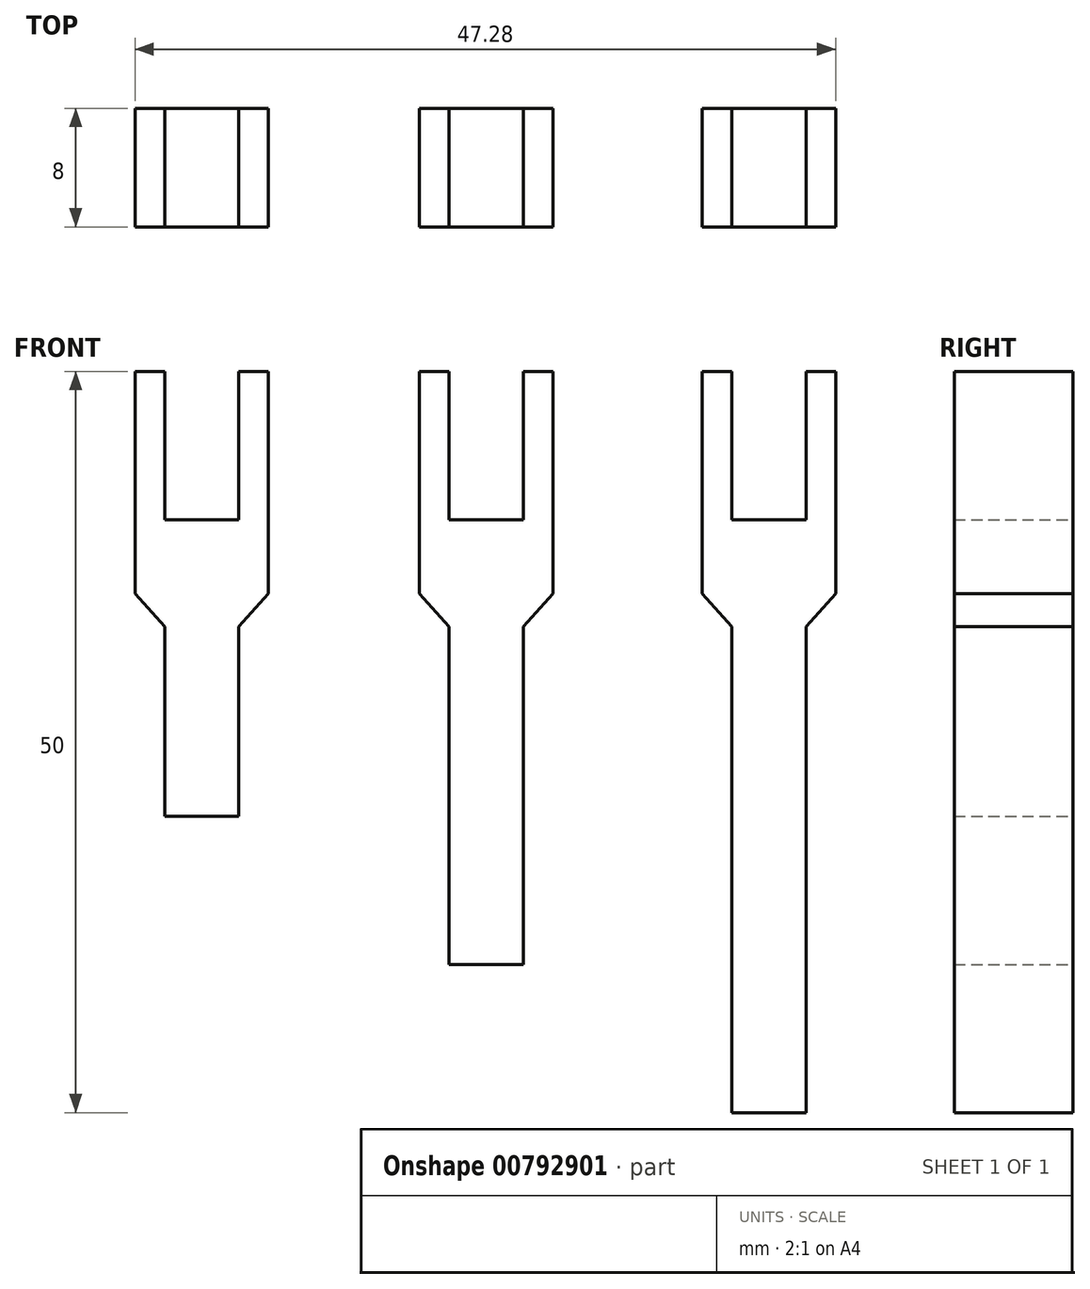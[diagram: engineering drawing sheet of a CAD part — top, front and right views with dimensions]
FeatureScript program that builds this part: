
annotation { "Feature Type Name" : "Feature", "Feature Type Description" : "" }
export const myFeature = defineFeature(function(context is Context, id is Id, definition is map)
    precondition{}
    {
        {
            var Q0;
            Q0=qCreatedBy(makeId("Front.planeOp"),FACE);
            var sketch = newSketch(context, id + "F0", { "sketchPlane" : qUnion([Q0])});
            skLineSegment(sketch, "E0.bottom", {"start": v(-2.5, -10) * mm, "end": v(2.5, -10) * mm});
            skLineSegment(sketch, "E0.top", {"start": v(-2.5, 10) * mm, "end": v(2.5, 10) * mm});
            skLineSegment(sketch, "E0.left", {"start": v(-2.5, -10) * mm, "end": v(-2.5, 2.78) * mm});
            skLineSegment(sketch, "E0.right", {"start": v(2.5, -10) * mm, "end": v(2.5, 2.78) * mm});
            skPoint(sketch, "E0.middle", {"position": v(0, 0) * mm});
            skLineSegment(sketch, "E1", {"start": v(-2.5, 10) * mm, "end": v(-2.5, 20) * mm});
            skLineSegment(sketch, "E2", {"start": v(-2.5, 20) * mm, "end": v(-4.5, 20) * mm});
            skLineSegment(sketch, "E3", {"start": v(-4.5, 20) * mm, "end": v(-4.5, 5) * mm});
            skLineSegment(sketch, "E4", {"start": v(-4.5, 5) * mm, "end": v(-2.5, 2.78) * mm});
            skLineSegment(sketch, "E5", {"start": v(0, 10) * mm, "end": v(0, 20) * mm, "construction": true});
            skLineSegment(sketch, "E6.MirrorCS", {"start": v(2.5, 10) * mm, "end": v(2.5, 20) * mm});
            skLineSegment(sketch, "E7.MirrorCS", {"start": v(2.5, 20) * mm, "end": v(4.5, 20) * mm});
            skLineSegment(sketch, "E8.MirrorCS", {"start": v(4.5, 20) * mm, "end": v(4.5, 5) * mm});
            skLineSegment(sketch, "E9.MirrorCS", {"start": v(4.5, 5) * mm, "end": v(2.5, 2.78) * mm});
            skLineSegment(sketch, "E10.top", {"start": v(16.7, 10) * mm, "end": v(21.7, 10) * mm});
            skPoint(sketch, "E10.middle", {"position": v(19.2, 0) * mm});
            skLineSegment(sketch, "E11", {"start": v(16.7, 10) * mm, "end": v(16.7, 20) * mm});
            skLineSegment(sketch, "E12", {"start": v(16.7, 20) * mm, "end": v(14.7, 20) * mm});
            skLineSegment(sketch, "E13", {"start": v(14.7, 20) * mm, "end": v(14.7, 5) * mm});
            skLineSegment(sketch, "E14", {"start": v(14.7, 5) * mm, "end": v(16.7, 2.78) * mm});
            skLineSegment(sketch, "E15", {"start": v(19.2, 10) * mm, "end": v(19.2, 20) * mm, "construction": true});
            skLineSegment(sketch, "E16.MirrorCS", {"start": v(21.7, 10) * mm, "end": v(21.7, 20) * mm});
            skLineSegment(sketch, "E17.MirrorCS", {"start": v(21.7, 20) * mm, "end": v(23.7, 20) * mm});
            skLineSegment(sketch, "E18.MirrorCS", {"start": v(23.7, 20) * mm, "end": v(23.7, 5) * mm});
            skLineSegment(sketch, "E19.MirrorCS", {"start": v(23.7, 5) * mm, "end": v(21.7, 2.78) * mm});
            skLineSegment(sketch, "E20", {"start": v(16.7, 2.78) * mm, "end": v(16.7, -20) * mm});
            skLineSegment(sketch, "E21", {"start": v(16.7, -20) * mm, "end": v(21.7, -20) * mm});
            skLineSegment(sketch, "E22", {"start": v(21.7, -20) * mm, "end": v(21.7, 2.78) * mm});
            skLineSegment(sketch, "E23.top", {"start": v(35.78, 10) * mm, "end": v(40.78, 10) * mm});
            skPoint(sketch, "E23.middle", {"position": v(38.28, 0) * mm});
            skLineSegment(sketch, "E24", {"start": v(35.78, 10) * mm, "end": v(35.78, 20) * mm});
            skLineSegment(sketch, "E25", {"start": v(35.78, 20) * mm, "end": v(33.78, 20) * mm});
            skLineSegment(sketch, "E26", {"start": v(33.78, 20) * mm, "end": v(33.78, 5) * mm});
            skLineSegment(sketch, "E27", {"start": v(33.78, 5) * mm, "end": v(35.78, 2.78) * mm});
            skLineSegment(sketch, "E28", {"start": v(38.28, 10) * mm, "end": v(38.28, 20) * mm, "construction": true});
            skLineSegment(sketch, "E29.MirrorCS", {"start": v(40.78, 10) * mm, "end": v(40.78, 20) * mm});
            skLineSegment(sketch, "E30.MirrorCS", {"start": v(40.78, 20) * mm, "end": v(42.78, 20) * mm});
            skLineSegment(sketch, "E31.MirrorCS", {"start": v(42.78, 20) * mm, "end": v(42.78, 5) * mm});
            skLineSegment(sketch, "E32.MirrorCS", {"start": v(42.78, 5) * mm, "end": v(40.78, 2.78) * mm});
            skLineSegment(sketch, "E33", {"start": v(35.78, 2.78) * mm, "end": v(35.78, -30) * mm});
            skLineSegment(sketch, "E34", {"start": v(35.78, -30) * mm, "end": v(40.78, -30) * mm});
            skLineSegment(sketch, "E35", {"start": v(40.78, -30) * mm, "end": v(40.78, 2.78) * mm});
            skSolve(sketch);
        }
        {
            var Q0;
            Q0=makeQuery(id+"F0.imprint","IMPRINT",FACE,{"disambiguationData":[TD([[makeQuery(id+"F0.imprint","IMPRINT",EDGE,{"derivedFrom":sQuery(id+"F0.wireOp",EDGE,"E0.bottom")}),1.0]])]});
            var Q1;
            Q1=makeQuery(id+"F0.imprint","IMPRINT",FACE,{"disambiguationData":[TD([[makeQuery(id+"F0.imprint","IMPRINT",EDGE,{"derivedFrom":sQuery(id+"F0.wireOp",EDGE,"E10.top")}),-1.0]])]});
            var Q2;
            Q2=makeQuery(id+"F0.imprint","IMPRINT",FACE,{"disambiguationData":[TD([[makeQuery(id+"F0.imprint","IMPRINT",EDGE,{"derivedFrom":sQuery(id+"F0.wireOp",EDGE,"E23.top")}),-1.0]])]});
            extrude(context, id + "F1", {"entities" : qUnion([Q0, Q1, Q2]), "depth" : 8 * mm, "offsetDistance" : 25 * mm});
        }
    });
